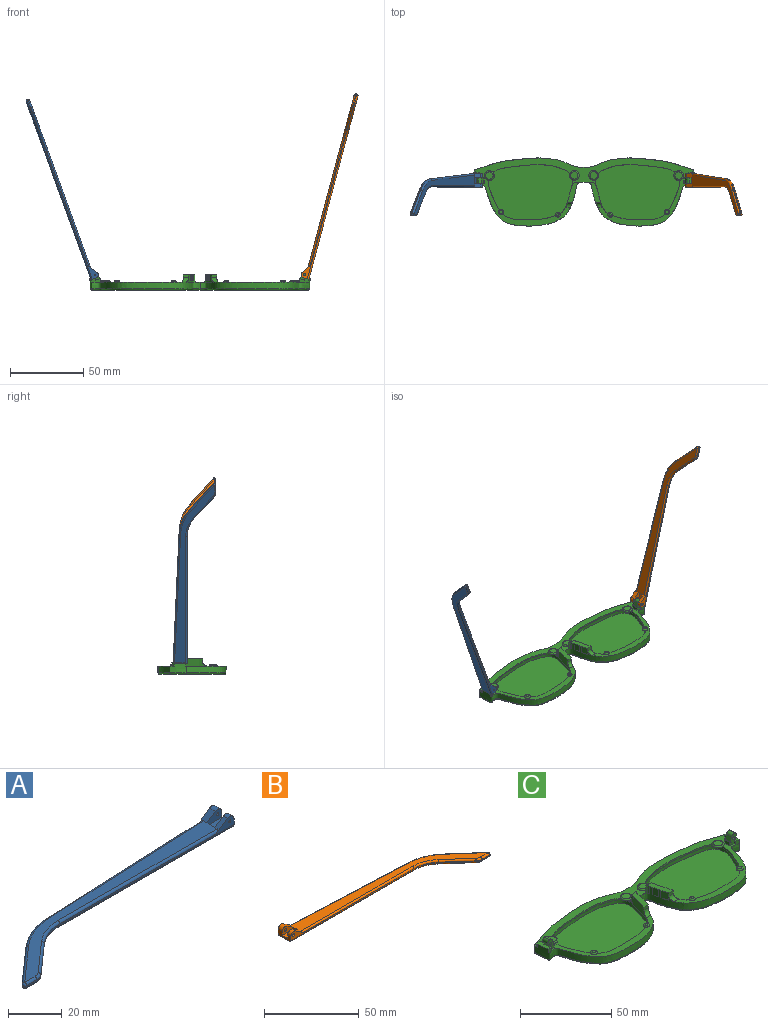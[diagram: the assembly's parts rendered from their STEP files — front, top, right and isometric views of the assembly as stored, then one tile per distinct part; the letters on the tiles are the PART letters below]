
ASSEMBLY  parts=3 mates=2
PART A: 43 faces, bbox 130.2x29.5x5.9 mm
  f0: plane 9.62x3.72mm, normal (1,0,0), area 24.7mm2, adj f1,f3,f4,f5,f10,f16,f18,f28
  f1: cylinder r=2.2mm len=3.45mm, axis (0,-1,0), area 11mm2, adj f0,f2,f4,f37
  f2: plane 6.01x3.91mm, normal (-0.55,0,0.84), area 12.7mm2, adj f1,f4,f9,f19,f37
  f3: plane 2.26x0.1mm, normal (0,0,1), area 0.1mm2, adj f0,f5,f18
  f4: plane 92.1x4.9mm, normal (0,-1,0), area 79.9mm2, adj f0,f1,f2,f14,f19,f36,f42
  f5: plane 93.42x4.13mm, normal (-0.04,1,0), area 64.8mm2, adj f0,f3,f11,f15,f17,f27,f28
  f6: plane 17.82x15.72mm, normal (-0.66,0.75,0), area 14.3mm2, adj f11,f12,f25,f30
  f7: plane 5.46x0.6mm, normal (0,-1,0), area 3.3mm2, adj f12,f13,f23,f32
  f8: plane 14.99x13.23mm, normal (0.66,-0.75,0), area 12mm2, adj f13,f14,f21,f34
  f9: plane 121.18x26.73mm, normal (0,0,1), area 627.7mm2, adj f2,f17,f19,f20,f21,f22,f23,f25
  f10: plane 129.1x27.08mm, normal (0,0,-1), area 686.5mm2, adj f0,f28,f29,f30,f32,f33,f34,f35
  f11: cylinder r=30mm len=18.52mm, axis (0,0,-1), area 12.2mm2, adj f5,f6,f26,f29
  f12: cylinder r=1mm len=1.75mm, axis (0,0,-1), area 1.5mm2, adj f6,f7,f24,f31
  f13: cylinder r=5mm len=3.31mm, axis (0,0,-1), area 2.2mm2, adj f7,f8,f22,f33
  f14: cylinder r=20mm len=13.23mm, axis (0,0,1), area 8.7mm2, adj f4,f8,f20,f35
  f15: plane 5.66x0.25mm, normal (0,0,-1), area 0.7mm2, adj f5,f17,f18
  f16: cylinder r=2.2mm len=3.45mm, axis (0,-1,0), area 14.8mm2, adj f0,f17,f18,f38
  f17: plane 6.01x3.91mm, normal (-0.55,0,0.84), area 16.9mm2, adj f5,f9,f15,f16,f18,f27,f38
  f18: plane 7.92x3.3mm, normal (0,1,0), area 15.9mm2, adj f0,f3,f15,f16,f17,f41
  f19: cylinder r=1mm len=84.18mm, axis (-1,0,0), area 131.4mm2, adj f2,f4,f9,f20
  f20: torus R=21mm, axis (0,0,1), area 23.1mm2, adj f9,f14,f19,f21
  f21: cylinder r=1mm len=15.65mm, axis (-0.75,-0.66,0), area 31.4mm2, adj f8,f9,f20,f22
  f22: torus R=4mm, axis (0,0,1), area 5.3mm2, adj f9,f13,f21,f23
  f23: cylinder r=1mm len=5.46mm, axis (-1,0,0), area 8.6mm2, adj f7,f9,f22,f24
  f24: sphere r=1mm, area 2.4mm2, adj f12,f23,f25
  f25: cylinder r=1mm len=18.48mm, axis (0.75,0.66,0), area 37.3mm2, adj f6,f9,f24,f26
  f26: torus R=29mm, axis (0,0,1), area 31.6mm2, adj f9,f11,f25,f27
  f27: cylinder r=1mm len=85.5mm, axis (1,0.04,0), area 133.5mm2, adj f5,f9,f17,f26
  f28: cylinder r=1mm len=93.46mm, axis (-1,-0.04,0), area 146.9mm2, adj f0,f5,f10,f29
  f29: torus R=29mm, axis (0,0,1), area 31.6mm2, adj f10,f11,f28,f30
  f30: cylinder r=1mm len=18.48mm, axis (-0.75,-0.66,0), area 37.3mm2, adj f6,f10,f29,f31
  f31: sphere r=1mm, area 2.4mm2, adj f12,f30,f32
  f32: cylinder r=1mm len=5.46mm, axis (1,0,0), area 8.6mm2, adj f7,f10,f31,f33
  f33: torus R=4mm, axis (0,0,1), area 5.3mm2, adj f10,f13,f32,f34
  f34: cylinder r=1mm len=15.65mm, axis (0.75,0.66,0), area 31.4mm2, adj f8,f10,f33,f35
  f35: torus R=21mm, axis (0,0,1), area 23.1mm2, adj f10,f14,f34,f36
  f36: cylinder r=1mm len=92.1mm, axis (1,0,0), area 144.7mm2, adj f0,f4,f10,f35
  f37: plane 7.92x4.7mm, normal (0,1,0), area 27mm2, adj f0,f1,f2,f39,f40,f42
  f38: plane 7.92x4.7mm, normal (0,-1,0), area 27mm2, adj f0,f16,f17,f39,f40,f41
  f39: plane 7.92x4.1mm, normal (0,0,1), area 32.5mm2, adj f0,f37,f38,f40
  f40: plane 4.1x1.4mm, normal (1,0,0), area 5.7mm2, adj f9,f37,f38,f39
  f41: cylinder r=0.5mm len=3.1mm, axis (0,-1,0), area 9.7mm2, adj f18,f38
  f42: cylinder r=0.5mm len=2.3mm, axis (0,-1,0), area 7.2mm2, adj f4,f37
PART B: 43 faces, bbox 130.2x29.5x5.9 mm
  f0: plane 9.62x3.72mm, normal (-1,0,0), area 24.7mm2, adj f1,f3,f4,f5,f10,f16,f18,f28
  f1: cylinder r=2.2mm len=3.45mm, axis (0,-1,0), area 11mm2, adj f0,f2,f4,f37
  f2: plane 6.01x3.91mm, normal (0.55,0,0.84), area 12.7mm2, adj f1,f4,f9,f19,f37
  f3: plane 2.26x0.1mm, normal (0,0,1), area 0.1mm2, adj f0,f5,f18
  f4: plane 92.1x4.9mm, normal (0,-1,0), area 78.2mm2, adj f0,f1,f2,f14,f19,f36,f42
  f5: plane 93.42x4.13mm, normal (0.04,1,0), area 64.8mm2, adj f0,f3,f11,f15,f17,f27,f28
  f6: plane 17.82x15.72mm, normal (0.66,0.75,0), area 14.3mm2, adj f11,f12,f25,f30
  f7: plane 5.46x0.6mm, normal (0,-1,0), area 3.3mm2, adj f12,f13,f23,f32
  f8: plane 14.99x13.23mm, normal (-0.66,-0.75,0), area 12mm2, adj f13,f14,f21,f34
  f9: plane 121.18x26.73mm, normal (0,0,1), area 627.7mm2, adj f2,f17,f19,f20,f21,f22,f23,f25
  f10: plane 129.1x27.08mm, normal (0,0,-1), area 686.5mm2, adj f0,f28,f29,f30,f32,f33,f34,f35
  f11: cylinder r=30mm len=18.52mm, axis (0,0,-1), area 12.2mm2, adj f5,f6,f26,f29
  f12: cylinder r=1mm len=1.75mm, axis (0,0,-1), area 1.5mm2, adj f6,f7,f24,f31
  f13: cylinder r=5mm len=3.31mm, axis (0,0,-1), area 2.2mm2, adj f7,f8,f22,f33
  f14: cylinder r=20mm len=13.23mm, axis (0,0,1), area 8.7mm2, adj f4,f8,f20,f35
  f15: plane 5.66x0.25mm, normal (0,0,-1), area 0.7mm2, adj f5,f17,f18
  f16: cylinder r=2.2mm len=3.45mm, axis (0,-1,0), area 14.8mm2, adj f0,f17,f18,f38
  f17: plane 6.01x3.91mm, normal (0.55,0,0.84), area 16.9mm2, adj f5,f9,f15,f16,f18,f27,f38
  f18: plane 7.92x3.3mm, normal (0,1,0), area 14.3mm2, adj f0,f3,f15,f16,f17,f41
  f19: cylinder r=1mm len=84.18mm, axis (1,0,0), area 131.4mm2, adj f2,f4,f9,f20
  f20: torus R=21mm, axis (0,0,1), area 23.1mm2, adj f9,f14,f19,f21
  f21: cylinder r=1mm len=15.65mm, axis (0.75,-0.66,0), area 31.4mm2, adj f8,f9,f20,f22
  f22: torus R=4mm, axis (0,0,1), area 5.3mm2, adj f9,f13,f21,f23
  f23: cylinder r=1mm len=5.46mm, axis (1,0,0), area 8.6mm2, adj f7,f9,f22,f24
  f24: sphere r=1mm, area 2.4mm2, adj f12,f23,f25
  f25: cylinder r=1mm len=18.48mm, axis (-0.75,0.66,0), area 37.3mm2, adj f6,f9,f24,f26
  f26: torus R=29mm, axis (0,0,1), area 31.6mm2, adj f9,f11,f25,f27
  f27: cylinder r=1mm len=85.5mm, axis (-1,0.04,0), area 133.5mm2, adj f5,f9,f17,f26
  f28: cylinder r=1mm len=93.46mm, axis (1,-0.04,0), area 146.9mm2, adj f0,f5,f10,f29
  f29: torus R=29mm, axis (0,0,1), area 31.6mm2, adj f10,f11,f28,f30
  f30: cylinder r=1mm len=18.48mm, axis (0.75,-0.66,0), area 37.3mm2, adj f6,f10,f29,f31
  f31: sphere r=1mm, area 2.4mm2, adj f12,f30,f32
  f32: cylinder r=1mm len=5.46mm, axis (-1,0,0), area 8.6mm2, adj f7,f10,f31,f33
  f33: torus R=4mm, axis (0,0,1), area 5.3mm2, adj f10,f13,f32,f34
  f34: cylinder r=1mm len=15.65mm, axis (-0.75,0.66,0), area 31.4mm2, adj f8,f10,f33,f35
  f35: torus R=21mm, axis (0,0,1), area 23.1mm2, adj f10,f14,f34,f36
  f36: cylinder r=1mm len=92.1mm, axis (-1,0,0), area 144.7mm2, adj f0,f4,f10,f35
  f37: plane 7.92x4.7mm, normal (0,1,0), area 25.4mm2, adj f0,f1,f2,f39,f40,f42
  f38: plane 7.92x4.7mm, normal (0,-1,0), area 25.4mm2, adj f0,f16,f17,f39,f40,f41
  f39: plane 7.92x4.1mm, normal (0,0,1), area 32.5mm2, adj f0,f37,f38,f40
  f40: plane 4.1x1.4mm, normal (-1,0,0), area 5.7mm2, adj f9,f37,f38,f39
  f41: cylinder r=0.88mm len=3.1mm, axis (0,-1,0), area 17mm2, adj f18,f38
  f42: cylinder r=0.88mm len=2.3mm, axis (0,-1,0), area 12.6mm2, adj f4,f37
PART C: 114 faces, bbox 151.4x47.8x12.9 mm
  f0: plane 2.1x0.76mm, normal (-1,0,0), area 0.8mm2, adj f23,f26,f33
  f1: plane 2.1x0.76mm, normal (-0.03,-1,0), area 0.8mm2, adj f13,f26,f33
  f2: plane 150.43x47.04mm, normal (0,0,1), area 1296.7mm2, adj f6,f7,f10,f12,f13,f20,f23,f24
  f3: plane 1.75x0.45mm, normal (0,0,1), area 0.1mm2, adj f10,f37
  f4: plane 4.82x1.62mm, normal (0,0,1), area 0.2mm2, adj f13,f35
  f5: plane 2.68x0.76mm, normal (0,0,1), area 0.9mm2, adj f13,f22
  f6: plane 6.81x5.07mm, normal (0,1,0), area 20.6mm2, adj f2,f20,f21,f24,f26,f27,f29,f30
  f7: plane 3.42x2.36mm, normal (0,-1,0), area 6mm2, adj f2,f20,f21,f25,f28
  f8: extruded ~57.14x37.48mm, area 351.6mm2, adj f9,f10
  f9: plane 57.55x37.59mm, normal (0,0,1), area 1777.9mm2, adj f8
  f10: extruded ~57.14x37.48mm, area 248.9mm2, adj f2,f3,f8,f36,f37,f40,f43,f46
  f11: plane 147.35x44.35mm, normal (0,0,-1), area 4768mm2, adj f14,f15,f17,f18,f70,f71,f73,f74
  f12: extruded ~39.05x6.4mm, area 180mm2, adj f2,f13,f14,f68
  f13: extruded ~74.67x45.89mm, area 802.2mm2, adj f1,f2,f4,f5,f12,f15,f16,f17
  f14: bspline ~40.29x7.4mm, area 62.8mm2, adj f11,f12,f15,f70
  f15: bspline ~54.19x9.96mm, area 56.5mm2, adj f11,f13,f14,f16
  f16: bspline ~1x0.97mm, area 0.4mm2, adj f13,f15,f18
  f17: bspline ~75.2x30.93mm, area 165.7mm2, adj f11,f13,f19,f73
  f18: bspline ~10.85x1.74mm, area 15.7mm2, adj f11,f13,f16,f19
  f19: bspline ~1.24x1mm, area 0.6mm2, adj f13,f17,f18
  f20: plane 4x2.36mm, normal (-1,0,0), area 9.5mm2, adj f2,f6,f7,f21
  f21: plane 4x0.45mm, normal (0.34,0,0.94), area 1.9mm2, adj f6,f7,f20,f27
  f22: plane 2.6x2.1mm, normal (0,-1,0), area 5.5mm2, adj f5,f13,f25,f26
  f23: plane 2.27x2.1mm, normal (0,1,0), area 4.8mm2, adj f0,f2,f24,f26
  f24: plane 3.28x2.1mm, normal (-1,0,0), area 6.9mm2, adj f2,f6,f23,f26
  f25: plane 2.1x1.38mm, normal (-1,0,0), area 2.9mm2, adj f2,f7,f22,f26,f28
  f26: plane 9.63x4.04mm, normal (0,0,1), area 25mm2, adj f0,f1,f6,f13,f22,f23,f24,f25
  f27: plane 4x3.31mm, normal (-0.94,0,0.34), area 14.1mm2, adj f6,f21,f28,f31
  f28: plane 5.69x4.62mm, normal (0,-1,0), area 14.7mm2, adj f7,f25,f26,f27,f29,f30,f31,f32
  f29: plane 4x2.21mm, normal (0.94,0,-0.34), area 9.4mm2, adj f6,f26,f28,f30
  f30: cylinder r=1.98mm len=4mm, axis (0,-1,0), area 11.5mm2, adj f6,f28,f29,f31
  f31: cylinder r=1.98mm len=4mm, axis (0,1,0), area 11.5mm2, adj f6,f27,f28,f30
  f32: cylinder r=0.88mm len=4mm, axis (0,-1,0), area 22mm2, adj f6,f28
  f33: cone r=1mm half-angle=20deg, axis (0,0,1), area 5mm2, adj f0,f1,f2,f26
  f34: extruded ~5x3.4mm, area 17.3mm2, adj f13,f40
  f35: extruded ~5x4.68mm, area 24.6mm2, adj f4,f13,f36,f40
  f36: plane 3.51x2mm, normal (0,-1,0), area 7mm2, adj f10,f35,f40,f53
  f37: extruded ~5x1.67mm, area 8.6mm2, adj f3,f10,f38,f40
  f38: plane 5x4.48mm, normal (0.11,0.99,0), area 22.5mm2, adj f2,f13,f37,f40
  f39: extruded ~5x0.57mm, area 3.3mm2, adj f13,f40
  f40: plane 13.69x8mm, normal (0,0,1), area 46.6mm2, adj f10,f13,f34,f35,f36,f37,f38,f39
  f41: cylinder r=3.33mm len=6.65mm, axis (0,0,-1), area 2.1mm2, adj f2,f43,f57
  f42: plane 5.05x5.05mm, normal (0,0,1), area 20.1mm2, adj f57
  f43: plane 5.72x3.94mm, normal (0,0,-1), area 14mm2, adj f10,f41
  f44: cylinder r=1.6mm len=3.19mm, axis (0,0,-1), area 1mm2, adj f2,f46,f56
  f45: plane 1.59x1.59mm, normal (0,0,1), area 2mm2, adj f56
  f46: plane 3.05x2.13mm, normal (0,0,-1), area 3.8mm2, adj f10,f44
  f47: cylinder r=1.88mm len=3.76mm, axis (0,0,-1), area 1.2mm2, adj f2,f49,f55
  f48: plane 2.16x2.16mm, normal (0,0,1), area 3.7mm2, adj f55
  f49: plane 3.26x3.09mm, normal (0,0,-1), area 5.4mm2, adj f10,f47
  f50: cylinder r=3.33mm len=6.65mm, axis (0,0,-1), area 2.1mm2, adj f2,f52,f54
  f51: plane 5.05x5.05mm, normal (0,0,1), area 20.1mm2, adj f54
  f52: plane 4.74x2.23mm, normal (0,0,-1), area 5.8mm2, adj f10,f50
  f53: cylinder r=3mm len=4.54mm, axis (1,0,0), area 16mm2, adj f2,f10,f13,f36
  f54: torus R=2.53mm, axis (0,0,1), area 24mm2, adj f50,f51
  f55: torus R=1.08mm, axis (0,0,1), area 12.6mm2, adj f47,f48
  f56: torus R=0.8mm, axis (0,0,1), area 10.3mm2, adj f44,f45
  f57: torus R=2.53mm, axis (0,0,1), area 24mm2, adj f41,f42
  f58: plane 2.1x0.76mm, normal (1,0,0), area 0.8mm2, adj f79,f82,f89
  f59: plane 2.1x0.76mm, normal (0.03,-1,0), area 0.8mm2, adj f69,f82,f89
  f60: plane 1.75x0.45mm, normal (0,0,1), area 0.1mm2, adj f67,f93
  f61: plane 4.85x1.65mm, normal (0,0,1), area 0.2mm2, adj f69,f91
  f62: plane 2.68x0.76mm, normal (0,0,1), area 0.9mm2, adj f69,f78
  f63: plane 6.81x5.07mm, normal (0,1,0), area 20.6mm2, adj f2,f76,f77,f80,f82,f83,f85,f86
  f64: plane 3.42x2.36mm, normal (0,-1,0), area 6mm2, adj f2,f76,f77,f81,f84
  f65: extruded ~57.14x37.48mm, area 351.6mm2, adj f66,f67
  f66: plane 57.55x37.59mm, normal (0,0,1), area 1777.9mm2, adj f65
  f67: extruded ~57.14x37.48mm, area 248.9mm2, adj f2,f60,f65,f92,f93,f96,f99,f102
  f68: extruded ~39.05x6.4mm, area 180mm2, adj f2,f12,f69,f70
  f69: extruded ~74.67x45.89mm, area 801.9mm2, adj f2,f13,f59,f61,f62,f68,f71,f72
  f70: bspline ~40.29x7.4mm, area 62.8mm2, adj f11,f14,f68,f71
  f71: bspline ~54.19x9.96mm, area 56.5mm2, adj f11,f69,f70,f72
  f72: bspline ~1x0.97mm, area 0.4mm2, adj f69,f71,f74
  f73: bspline ~75.2x30.93mm, area 165.7mm2, adj f11,f17,f69,f75
  f74: bspline ~10.85x1.74mm, area 15.7mm2, adj f11,f69,f72,f75
  f75: bspline ~1.24x1mm, area 0.6mm2, adj f69,f73,f74
  f76: plane 4x2.36mm, normal (1,0,0), area 9.5mm2, adj f2,f63,f64,f77
  f77: plane 4x0.45mm, normal (-0.34,0,0.94), area 1.9mm2, adj f63,f64,f76,f83
  f78: plane 2.6x2.1mm, normal (0,-1,0), area 5.5mm2, adj f62,f69,f81,f82
  f79: plane 2.27x2.1mm, normal (0,1,0), area 4.8mm2, adj f2,f58,f80,f82
  f80: plane 3.28x2.1mm, normal (1,0,0), area 6.9mm2, adj f2,f63,f79,f82
  f81: plane 2.1x1.38mm, normal (1,0,0), area 2.9mm2, adj f2,f64,f78,f82,f84
  f82: plane 9.63x4.04mm, normal (0,0,1), area 25mm2, adj f58,f59,f63,f69,f78,f79,f80,f81
  f83: plane 4x3.31mm, normal (0.94,0,0.34), area 14.1mm2, adj f63,f77,f84,f87
  f84: plane 5.69x4.62mm, normal (0,-1,0), area 14.7mm2, adj f64,f81,f82,f83,f85,f86,f87,f88
  f85: plane 4x2.21mm, normal (-0.94,0,-0.34), area 9.4mm2, adj f63,f82,f84,f86
  f86: cylinder r=1.98mm len=4mm, axis (0,-1,0), area 11.5mm2, adj f63,f84,f85,f87
  f87: cylinder r=1.98mm len=4mm, axis (0,1,0), area 11.5mm2, adj f63,f83,f84,f86
  f88: cylinder r=0.88mm len=4mm, axis (0,-1,0), area 22mm2, adj f63,f84
  f89: cone r=1mm half-angle=20deg, axis (0,0,1), area 5mm2, adj f2,f58,f59,f82
  f90: extruded ~5x3.4mm, area 17.3mm2, adj f69,f96
  f91: extruded ~5x4.68mm, area 24.6mm2, adj f61,f69,f92,f96
  f92: plane 3.51x2mm, normal (0,-1,0), area 7mm2, adj f67,f91,f96,f109
  f93: extruded ~5x1.67mm, area 8.6mm2, adj f60,f67,f94,f96
  f94: plane 5x4.48mm, normal (-0.11,0.99,0), area 22.5mm2, adj f2,f69,f93,f96
  f95: extruded ~5x0.57mm, area 3.3mm2, adj f69,f96
  f96: plane 13.69x8mm, normal (0,0,1), area 46.6mm2, adj f67,f69,f90,f91,f92,f93,f94,f95
  f97: cylinder r=3.33mm len=6.65mm, axis (0,0,-1), area 2.1mm2, adj f2,f99,f113
  f98: plane 5.05x5.05mm, normal (0,0,1), area 20.1mm2, adj f113
  f99: plane 5.72x3.94mm, normal (0,0,-1), area 14mm2, adj f67,f97
  f100: cylinder r=1.6mm len=3.19mm, axis (0,0,-1), area 1mm2, adj f2,f102,f112
  f101: plane 1.59x1.59mm, normal (0,0,1), area 2mm2, adj f112
  f102: plane 3.05x2.13mm, normal (0,0,-1), area 3.8mm2, adj f67,f100
  f103: cylinder r=1.88mm len=3.76mm, axis (0,0,-1), area 1.2mm2, adj f2,f105,f111
  f104: plane 2.16x2.16mm, normal (0,0,1), area 3.7mm2, adj f111
  f105: plane 3.26x3.09mm, normal (0,0,-1), area 5.4mm2, adj f67,f103
  f106: cylinder r=3.33mm len=6.65mm, axis (0,0,-1), area 2.1mm2, adj f2,f108,f110
  f107: plane 5.05x5.05mm, normal (0,0,1), area 20.1mm2, adj f110
  f108: plane 4.74x2.23mm, normal (0,0,-1), area 5.8mm2, adj f67,f106
  f109: cylinder r=3mm len=4.54mm, axis (-1,0,0), area 16mm2, adj f2,f67,f69,f92
  f110: torus R=2.53mm, axis (0,0,1), area 24mm2, adj f106,f107
  f111: torus R=1.08mm, axis (0,0,1), area 12.6mm2, adj f103,f104
  f112: torus R=0.8mm, axis (0,0,1), area 10.3mm2, adj f100,f101
  f113: torus R=2.53mm, axis (0,0,1), area 24mm2, adj f97,f98
PLACE A rot(axis=(0,1,0),70deg) t=(-85.2,-5.75,55.85)mm
PLACE B rot(axis=(0,-1,0),75deg) t=(68.2,-5.75,-61.61)mm
PLACE C t=(10.15,-1.13,-7.02)mm
MATE revolute A.f1 <-> C.f87  axis (0,-1,0) through (-61.32,2.72,1.06)mm
MATE revolute B.f41 <-> C.f30  axis (0,-1,0) through (81.2,2.72,1.21)mm
